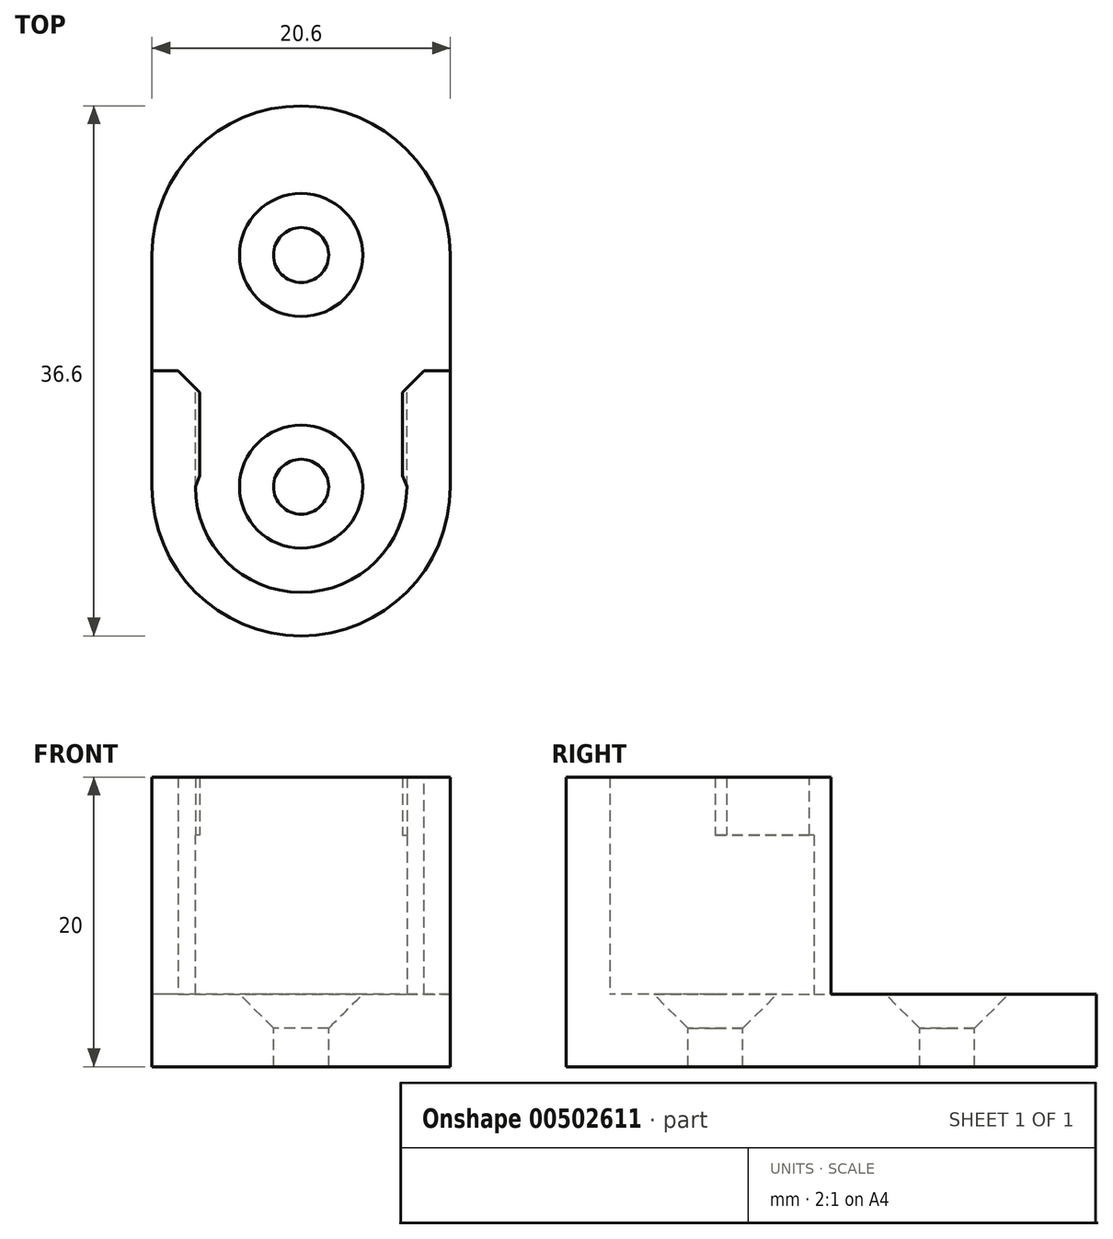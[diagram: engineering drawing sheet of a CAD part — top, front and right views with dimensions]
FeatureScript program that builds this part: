
annotation { "Feature Type Name" : "Feature", "Feature Type Description" : "" }
export const myFeature = defineFeature(function(context is Context, id is Id, definition is map)
    precondition{}
    {
        {
            var Q0;
            Q0=qCreatedBy(makeId("Top.planeOp"),FACE);
            var sketch = newSketch(context, id + "F0", { "sketchPlane" : qUnion([Q0])});
            skArc(sketch, "E0", {"start": v(-7.3, 0) * mm, "mid": v(0, -7.3) * mm, "end": v(7.3, 0) * mm});
            skLineSegment(sketch, "E1", {"start": v(-7.3, 0) * mm, "end": v(-7.3, 8) * mm});
            skLineSegment(sketch, "E2", {"start": v(-7.3, 8) * mm, "end": v(-10.3, 8) * mm});
            skLineSegment(sketch, "E3", {"start": v(-10.3, 8) * mm, "end": v(-10.3, 0) * mm});
            skLineSegment(sketch, "E4", {"start": v(0, 0) * mm, "end": v(0, 16) * mm, "construction": true});
            skLineSegment(sketch, "E5.MirrorCS", {"start": v(7.3, 0) * mm, "end": v(7.3, 8) * mm});
            skLineSegment(sketch, "E6.MirrorCS", {"start": v(7.3, 8) * mm, "end": v(10.3, 8) * mm});
            skLineSegment(sketch, "E7.MirrorCS", {"start": v(10.3, 8) * mm, "end": v(10.3, 0) * mm});
            skArc(sketch, "E8.0", {"start": v(-10.3, 0) * mm, "mid": v(0, -10.3) * mm, "end": v(10.3, 0) * mm});
            skLineSegment(sketch, "E9.MirrorCS", {"start": v(-10.3, 8) * mm, "end": v(-10.3, 16) * mm});
            skLineSegment(sketch, "E10.MirrorCS", {"start": v(10.3, 8) * mm, "end": v(10.3, 16) * mm});
            skArc(sketch, "E11.MirrorCS", {"start": v(-10.3, 16) * mm, "mid": v(0, 26.3) * mm, "end": v(10.3, 16) * mm});
            skCircle(sketch, "E12", {"center": v(0, -0.2) * mm, "radius": 7.1 * mm, "construction": true});
            skPoint(sketch, "E12.centerSnap0", {"position": v(0, -10.3) * mm});
            skLineSegment(sketch, "E13.0", {"start": v(-7, 0) * mm, "end": v(-7, 16) * mm, "construction": true});
            skLineSegment(sketch, "E14.0", {"start": v(7, 0) * mm, "end": v(7, 16) * mm, "construction": true});
            skLineSegment(sketch, "E15", {"start": v(-7.3, 8) * mm, "end": v(-7, 8) * mm});
            skLineSegment(sketch, "E16", {"start": v(-7, 8) * mm, "end": v(-7, 0.78) * mm});
            skLineSegment(sketch, "E17", {"start": v(-7, 0.78) * mm, "end": v(-7.3, 0) * mm});
            skLineSegment(sketch, "E18.MirrorCS", {"start": v(7, 8) * mm, "end": v(7, 0.78) * mm});
            skLineSegment(sketch, "E19.MirrorCS", {"start": v(7.3, 8) * mm, "end": v(7, 8) * mm});
            skLineSegment(sketch, "E20.MirrorCS", {"start": v(7, 0.78) * mm, "end": v(7.3, 0) * mm});
            skSolve(sketch);
        }
        {
            var Q0;
            Q0=makeQuery(id+"F0.imprint","IMPRINT",FACE,{"disambiguationData":[TD([[makeQuery(id+"F0.imprint","IMPRINT",EDGE,{"derivedFrom":sQuery(id+"F0.wireOp",EDGE,"E0")}),-1.0]])]});
            extrude(context, id + "F1", {"entities" : qUnion([Q0]), "depth" : 15 * mm, "hasSecondDirection" : true, "secondDirectionOppositeDirection" : true, "secondDirectionDepth" : 5 * mm});
        }
        {
            var Q0;
            Q0=makeQuery(id+"F0.imprint","IMPRINT",FACE,{"disambiguationData":[TD([[makeQuery(id+"F0.imprint","IMPRINT",EDGE,{"derivedFrom":sQuery(id+"F0.wireOp",EDGE,"E1")}),-1.0]])]});
            var Q1;
            Q1=makeQuery(id+"F0.imprint","IMPRINT",FACE,{"disambiguationData":[TD([[makeQuery(id+"F0.imprint","IMPRINT",EDGE,{"derivedFrom":sQuery(id+"F0.wireOp",EDGE,"E5.MirrorCS")}),1.0]])]});
            extrude(context, id + "F2", {"entities" : qUnion([Q0, Q1]), "operationType" : NewBodyOperationType.ADD, "depth" : 15 * mm, "hasSecondDirection" : true, "secondDirectionOppositeDirection" : false, "secondDirectionDepth" : 11 * mm});
        }
        {
            var Q0;
            Q0=makeQuery(id+"F0.imprint","IMPRINT",FACE,{"disambiguationData":[TD([[makeQuery(id+"F0.imprint","IMPRINT",EDGE,{"derivedFrom":sQuery(id+"F0.wireOp",EDGE,"E1")}),-1.0]])]});
            var Q1;
            Q1=makeQuery(id+"F0.imprint","IMPRINT",FACE,{"disambiguationData":[TD([[makeQuery(id+"F0.imprint","IMPRINT",EDGE,{"derivedFrom":sQuery(id+"F0.wireOp",EDGE,"E0")}),1.0]])]});
            var Q2;
            Q2=makeQuery(id+"F0.imprint","IMPRINT",FACE,{"disambiguationData":[TD([[makeQuery(id+"F0.imprint","IMPRINT",EDGE,{"derivedFrom":sQuery(id+"F0.wireOp",EDGE,"E5.MirrorCS")}),1.0]])]});
            extrude(context, id + "F3", {"entities" : qUnion([Q0, Q1, Q2]), "operationType" : NewBodyOperationType.ADD, "oppositeDirection" : true, "depth" : 5 * mm});
        }
        {
            var Q0;
            Q0=sQuery(id+"F0.wireOp",VERTEX,"E4.end");
            var Q1;
            Q1=sQuery(id+"F0.wireOp",VERTEX,"E8.0.center");
            var Q2;
            Q2=makeQuery(id+"F1.opExtrude","SWEPT_BODY",BODY,{"disambiguationData":[OSD([sQuery(id+"F0.wireOp",EDGE,"E0"),sQuery(id+"F0.wireOp",EDGE,"E1"),sQuery(id+"F0.wireOp",EDGE,"E2"),sQuery(id+"F0.wireOp",EDGE,"E3"),sQuery(id+"F0.wireOp",EDGE,"E5.MirrorCS"),sQuery(id+"F0.wireOp",EDGE,"E6.MirrorCS"),sQuery(id+"F0.wireOp",EDGE,"E7.MirrorCS"),sQuery(id+"F0.wireOp",EDGE,"E8.0")])]});
            hole(context, id + "F4", {"style" : HoleStyle.C_SINK, "endStyle" : HoleEndStyle.THROUGH, "holeDiameter" : 3.8 * mm, "cSinkDiameter" : 8.5 * mm, "cSinkAngle" : 90 * degree, "isTappedThrough" : true, "tappedDepth" : 12 * mm, "tapClearance" : 3, "locations" : qUnion([Q0, Q1]), "scope" : qUnion([Q2])});
        }
        {
            var Q0;
            Q0=makeQuery(id+"F2.opExtrude","SWEPT_EDGE",EDGE,{"disambiguationData":[OSD([sQuery(id+"F0.wireOp",EDGE,"E15"),sQuery(id+"F0.wireOp",EDGE,"E16")])]});
            var Q1;
            Q1=makeQuery(id+"F2.opExtrude","SWEPT_EDGE",EDGE,{"disambiguationData":[OSD([sQuery(id+"F0.wireOp",EDGE,"E18.MirrorCS"),sQuery(id+"F0.wireOp",EDGE,"E19.MirrorCS")])]});
            chamfer(context, id + "F5", {"entities" : qUnion([Q0, Q1]), "width" : 1.5 * mm, "tangentPropagation" : true});
        }
    });
